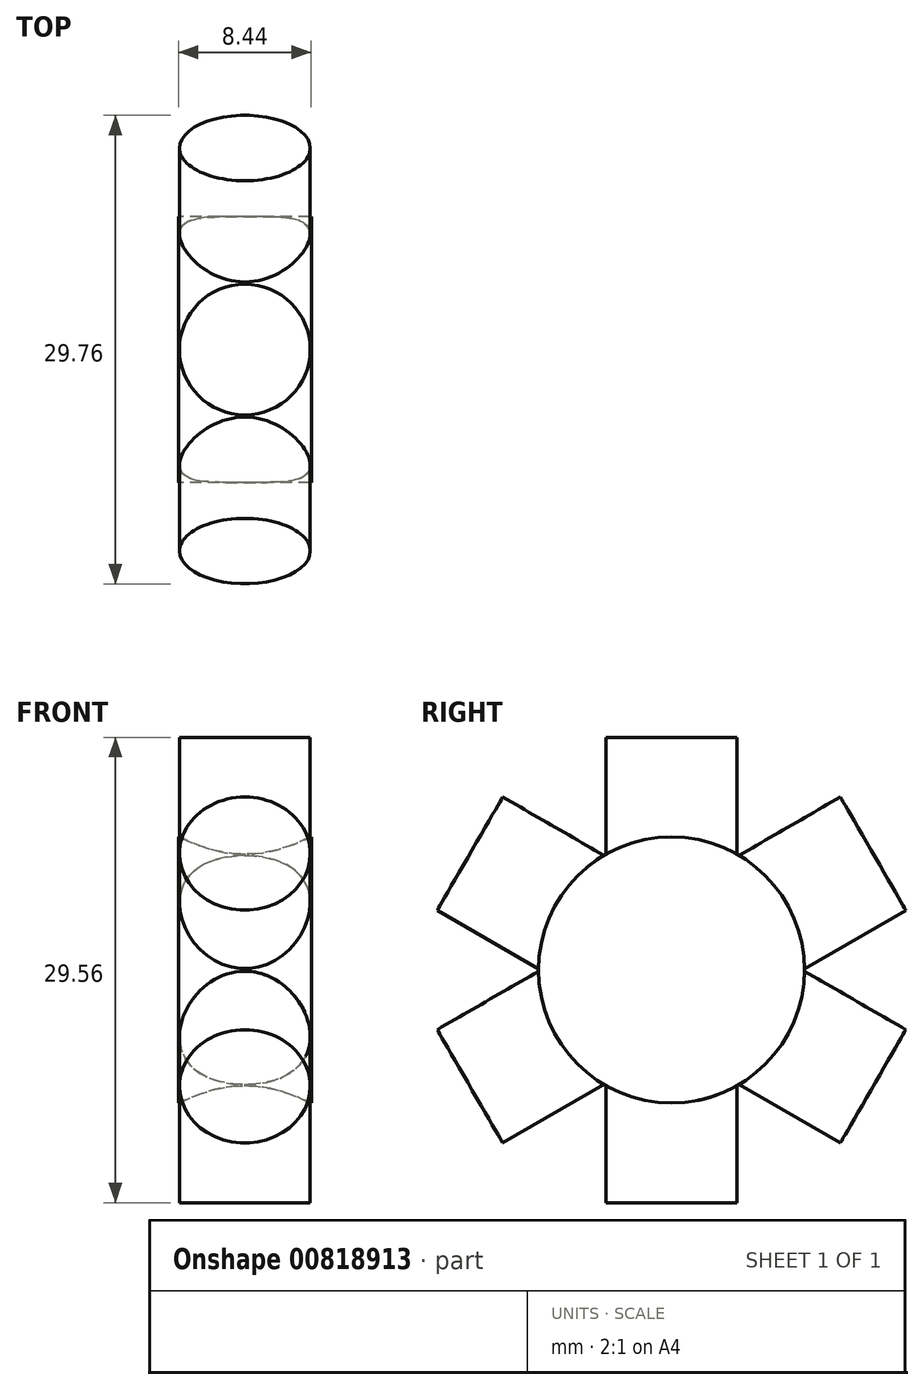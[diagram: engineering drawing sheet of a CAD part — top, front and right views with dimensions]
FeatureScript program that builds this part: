
annotation { "Feature Type Name" : "Feature", "Feature Type Description" : "" }
export const myFeature = defineFeature(function(context is Context, id is Id, definition is map)
    precondition{}
    {
        {
            var Q0;
            Q0=qCreatedBy(makeId("Right.planeOp"),FACE);
            var sketch = newSketch(context, id + "F0", { "sketchPlane" : qUnion([Q0])});
            skLineSegment(sketch, "E0.bottom", {"start": v(0, 14.78) * mm, "end": v(-4.16, 14.78) * mm});
            skLineSegment(sketch, "E0.top", {"start": v(0, -14.78) * mm, "end": v(-4.16, -14.78) * mm});
            skLineSegment(sketch, "E0.left", {"start": v(0, 14.78) * mm, "end": v(0, -14.78) * mm});
            skLineSegment(sketch, "E0.right", {"start": v(-4.16, 14.78) * mm, "end": v(-4.16, -14.78) * mm});
            skPoint(sketch, "E0.middle", {"position": v(-2.08, 0) * mm});
            skSolve(sketch);
        }
        {
            var Q0;
            Q0=qCreatedBy(makeId("Right.planeOp"),FACE);
            var sketch = newSketch(context, id + "F1", { "sketchPlane" : qUnion([Q0])});
            skLineSegment(sketch, "E1.bottom", {"start": v(12.8, 7.39) * mm, "end": v(10.72, 10.99) * mm});
            skLineSegment(sketch, "E1.top", {"start": v(-12.8, -7.39) * mm, "end": v(-14.88, -3.8) * mm});
            skLineSegment(sketch, "E1.left", {"start": v(12.8, 7.39) * mm, "end": v(-12.8, -7.39) * mm});
            skLineSegment(sketch, "E1.right", {"start": v(10.72, 10.99) * mm, "end": v(-14.88, -3.8) * mm});
            skPoint(sketch, "E1.middle", {"position": v(-1.04, 1.8) * mm});
            skSolve(sketch);
        }
        {
            var Q0;
            Q0=qCreatedBy(makeId("Right.planeOp"),FACE);
            var sketch = newSketch(context, id + "F2", { "sketchPlane" : qUnion([Q0])});
            skLineSegment(sketch, "E2.bottom", {"start": v(12.8, -7.39) * mm, "end": v(14.88, -3.8) * mm});
            skLineSegment(sketch, "E2.top", {"start": v(-12.8, 7.39) * mm, "end": v(-10.72, 10.99) * mm});
            skLineSegment(sketch, "E2.left", {"start": v(12.8, -7.39) * mm, "end": v(-12.8, 7.39) * mm});
            skLineSegment(sketch, "E2.right", {"start": v(14.88, -3.8) * mm, "end": v(-10.72, 10.99) * mm});
            skPoint(sketch, "E2.middle", {"position": v(1.04, 1.8) * mm});
            skSolve(sketch);
        }
        {
            var Q0;
            Q0=qSketchRegion(id+"F0",true);
            var Q1;
            Q1=sQuery(id+"F0.wireOp",EDGE,"E0.left");
            revolve(context, id + "F3", {"surfaceOperationType" : NewSurfaceOperationType.NEW, "entities" : qUnion([Q0]), "axis" : qUnion([Q1]), "revolveType" : RevolveType.FULL});
        }
        {
            var Q0;
            Q0 = qSketchRegion(id + "F1", true);
            var Q1;
            Q1=sQuery(id+"F1.wireOp",EDGE,"E1.left");
            revolve(context, id + "F4", {"operationType" : NewBodyOperationType.ADD, "surfaceOperationType" : NewSurfaceOperationType.NEW, "entities" : qUnion([Q0]), "axis" : qUnion([Q1]), "revolveType" : RevolveType.FULL});
        }
        {
            var Q0;
            Q0=makeQuery(id+"F2.imprint","IMPRINT",FACE,{"disambiguationData":[TD([[makeQuery(id+"F2.imprint","IMPRINT",EDGE,{"derivedFrom":sQuery(id+"F2.wireOp",EDGE,"E2.bottom")}),1.0]])]});
            var Q1;
            Q1=sQuery(id+"F2.wireOp",EDGE,"E2.left");
            revolve(context, id + "F5", {"operationType" : NewBodyOperationType.ADD, "surfaceOperationType" : NewSurfaceOperationType.NEW, "entities" : qUnion([Q0]), "axis" : qUnion([Q1]), "revolveType" : RevolveType.FULL});
        }
        {
            var Q0;
            Q0=qCreatedBy(makeId("Right.planeOp"),FACE);
            var sketch = newSketch(context, id + "F6", { "sketchPlane" : qUnion([Q0])});
            skCircle(sketch, "E3", {"center": v(0, 0) * mm, "radius": 8.45 * mm});
            skSolve(sketch);
        }
        {
            var Q0;
            Q0=qSketchRegion(id+"F6",true);
            extrude(context, id + "F7", {"entities" : qUnion([Q0]), "operationType" : NewBodyOperationType.ADD, "endBound" : BoundingType.SYMMETRIC, "depth" : 8.45 * mm, "offsetDistance" : 25.4 * mm});
        }
    });
